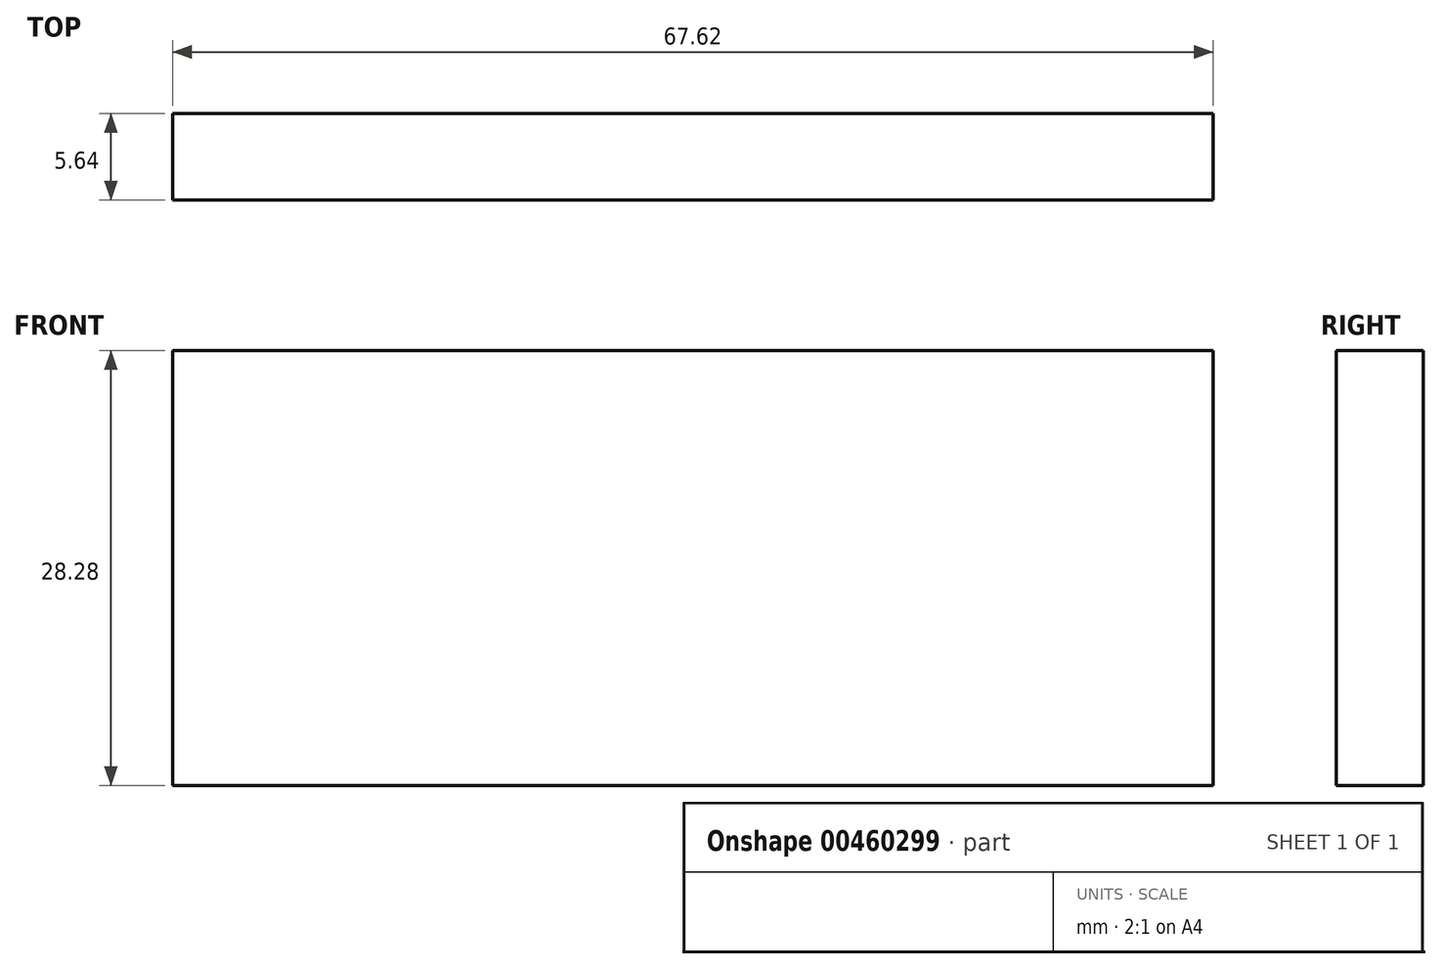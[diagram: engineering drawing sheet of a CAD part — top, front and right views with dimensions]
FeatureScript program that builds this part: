
annotation { "Feature Type Name" : "Feature", "Feature Type Description" : "" }
export const myFeature = defineFeature(function(context is Context, id is Id, definition is map)
    precondition{}
    {
        {
            var Q0;
            Q0=qCreatedBy(makeId("Front.planeOp"),FACE);
            var sketch = newSketch(context, id + "F0", { "sketchPlane" : qUnion([Q0])});
            skLineSegment(sketch, "E0.bottom", {"start": v(-33.81, 14.14) * mm, "end": v(33.81, 14.14) * mm});
            skLineSegment(sketch, "E0.top", {"start": v(-33.81, -14.14) * mm, "end": v(33.81, -14.14) * mm});
            skLineSegment(sketch, "E0.left", {"start": v(-33.81, 14.14) * mm, "end": v(-33.81, -14.14) * mm});
            skLineSegment(sketch, "E0.right", {"start": v(33.81, 14.14) * mm, "end": v(33.81, -14.14) * mm});
            skPoint(sketch, "E0.middle", {"position": v(0, 0) * mm});
            skSolve(sketch);
        }
        {
            var Q0;
            Q0=makeQuery(id+"F0.imprint","IMPRINT",FACE,{"disambiguationData":[TD([[makeQuery(id+"F0.imprint","IMPRINT",EDGE,{"derivedFrom":sQuery(id+"F0.wireOp",EDGE,"E0.bottom")}),-1.0]])]});
            extrude(context, id + "F1", {"entities" : qUnion([Q0]), "depth" : 5.64 * mm});
        }
    });
